# Revit family: GEN_A3-M-Ladder2
name_source: partatom
category: Specialty Equipment
revit_build: Autodesk Revit 2016 (Build: 20150220_1215(x64)
units: mm (PartAtom-declared; Revit-internal decimal feet)

## family parameters
Always vertical = Yes
Cut with Voids When Loaded = No
Host = Wall
OmniClass Number = 23.30.70.17
OmniClass Title = Ladders
Part Type = Normal
Room Calculation Point = No
Round Connector Dimension = Use Diameter
Shared = No

## types (2) — shared parameters
Guardrail Height = 1070 mm  [stored 3.5105 ft]
Guardrail Length = 510 mm  [stored 1.67323 ft]
Half Guardrail Height = 535 mm  [stored 1.75525 ft]
Rung Radius = 10 mm  [stored 0.0328084 ft]
Side Rail Thickness = 76 mm
Side Rail Width = 10 mm  [stored 0.0328084 ft]

## type names (no varying parameters)
- Standard
- M Ladder

note: [stored X ft] marks values corroborated as IEEE doubles in the binary element streams (Revit-internal decimal feet)

## geometry (parser evidence)
native form markers: Sweep x5
no freeform markers — native parametric forms only
